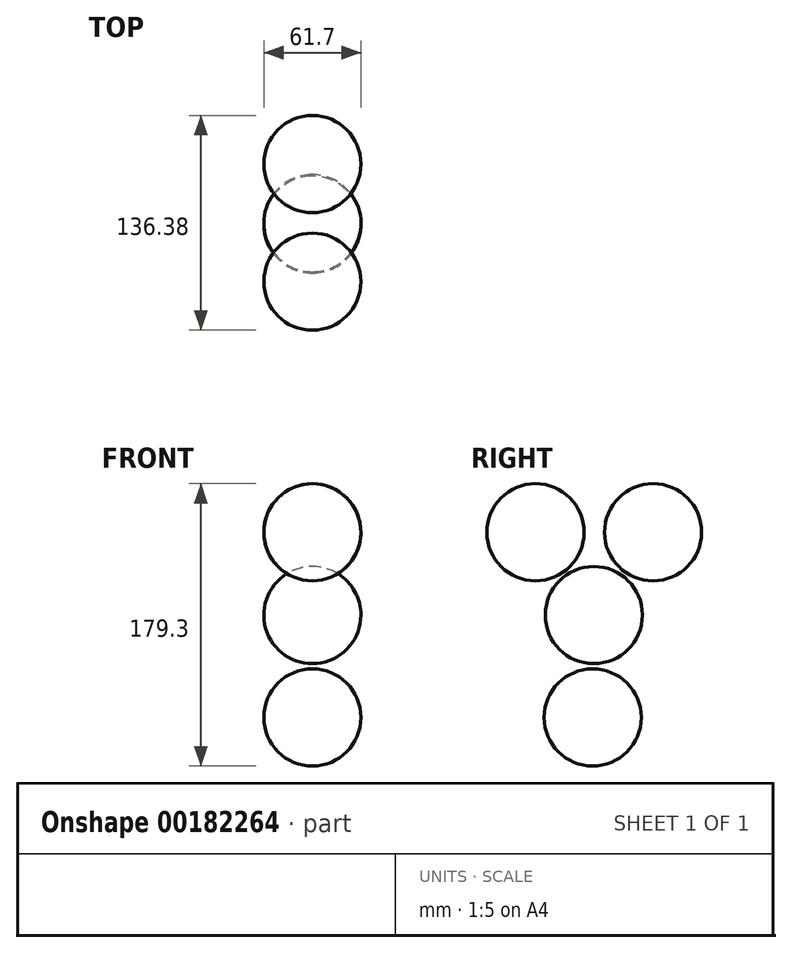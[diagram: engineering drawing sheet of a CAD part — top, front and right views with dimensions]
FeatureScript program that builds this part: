
annotation { "Feature Type Name" : "Feature", "Feature Type Description" : "" }
export const myFeature = defineFeature(function(context is Context, id is Id, definition is map)
    precondition{}
    {
        {
            var Q0;
            Q0=qCreatedBy(makeId("Top.planeOp"),FACE);
            var sketch = newSketch(context, id + "F0", { "sketchPlane" : qUnion([Q0])});
            skArc(sketch, "E0", {"start": v(0, 30.85) * mm, "mid": v(-30.85, 0) * mm, "end": v(0, -30.85) * mm});
            skLineSegment(sketch, "E1", {"start": v(0, 30.85) * mm, "end": v(0, -30.85) * mm});
            skSolve(sketch);
        }
        {
            var Q0;
            Q0=makeQuery(id+"F0.imprint","IMPRINT",FACE,{"disambiguationData":[TD([[makeQuery(id+"F0.imprint","IMPRINT",EDGE,{"derivedFrom":sQuery(id+"F0.wireOp",EDGE,"E0")}),1.0]])]});
            var Q1;
            Q1=sQuery(id+"F0.wireOp",EDGE,"E1");
            revolve(context, id + "F1", {"entities" : qUnion([Q0]), "axis" : qUnion([Q1]), "revolveType" : RevolveType.FULL});
        }
        {
            var Q0;
            Q0=makeQuery(id+"F1.opRevolve","SWEPT_BODY",BODY,{"disambiguationData":[OSD([sQuery(id+"F0.wireOp",EDGE,"E0"),sQuery(id+"F0.wireOp",EDGE,"E1")])]});
            transform(context, id + "F2", {"entities" : qUnion([Q0]), "transformType" : TransformType.TRANSLATION_3D, "dx" : 0 * mm, "dy" : 37.34 * mm, "dz" : 104.14 * mm, "makeCopy" : false});
        }
        {
            var Q0;
            Q0=makeQuery(id+"F1.opRevolve","SWEPT_BODY",BODY,{"disambiguationData":[OSD([sQuery(id+"F0.wireOp",EDGE,"E0"),sQuery(id+"F0.wireOp",EDGE,"E1")])]});
            var Q1;
            Q1=qCreatedBy(makeId("Front.planeOp"),FACE);
            mirror(context, id + "F3", {"entities" : qUnion([Q0]), "mirrorPlane" : qUnion([Q1])});
        }
        {
            var Q0;
            Q0=makeQuery(id+"F1.opRevolve","SWEPT_BODY",BODY,{"disambiguationData":[OSD([sQuery(id+"F0.wireOp",EDGE,"E0"),sQuery(id+"F0.wireOp",EDGE,"E1")])]});
            transform(context, id + "F4", {"entities" : qUnion([Q0]), "transformType" : TransformType.TRANSLATION_3D, "dx" : 0 * mm, "dy" : -37.6 * mm, "dz" : -52.58 * mm, "makeCopy" : true});
        }
        {
            var Q0;
            Q0=makeQuery(id+"F4.opPattern","COPY",BODY,{"derivedFrom":makeQuery(id+"F1.opRevolve","SWEPT_BODY",BODY,{"disambiguationData":[OSD([sQuery(id+"F0.wireOp",EDGE,"E0"),sQuery(id+"F0.wireOp",EDGE,"E1")])]}),"instanceName":"1"});
            transform(context, id + "F5", {"entities" : qUnion([Q0]), "transformType" : TransformType.TRANSLATION_3D, "dx" : 0 * mm, "dy" : -0.76 * mm, "dz" : -65.02 * mm, "makeCopy" : true});
        }
    });
